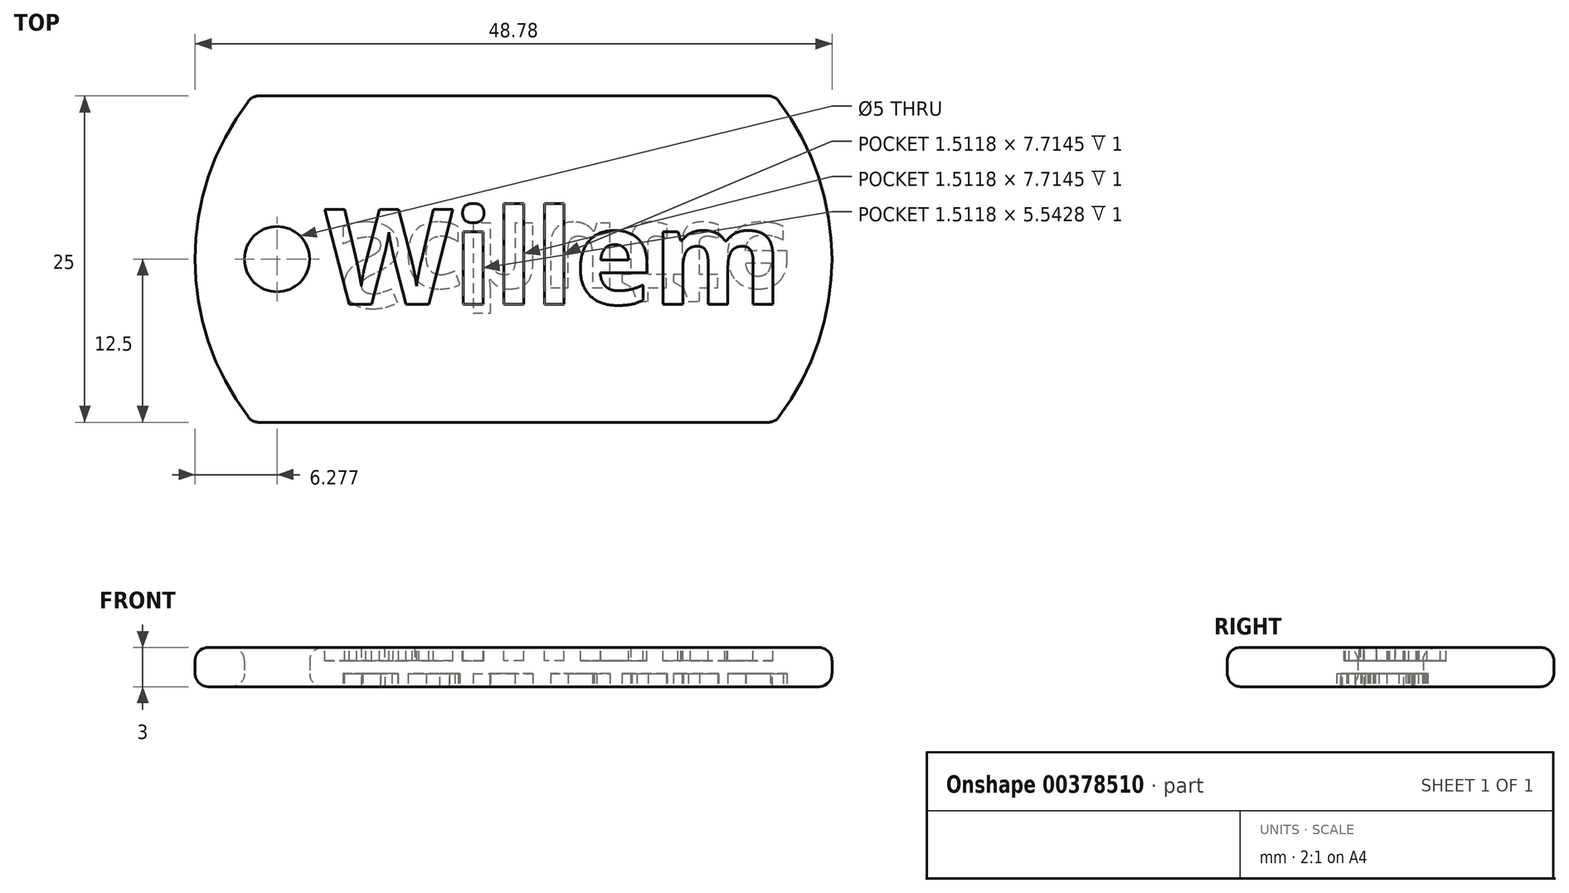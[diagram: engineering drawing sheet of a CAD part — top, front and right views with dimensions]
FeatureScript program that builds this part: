
annotation { "Feature Type Name" : "Feature", "Feature Type Description" : "" }
export const myFeature = defineFeature(function(context is Context, id is Id, definition is map)
    precondition{}
    {
        {
            var Q0;
            Q0=qCreatedBy(makeId("Top.planeOp"),FACE);
            var sketch = newSketch(context, id + "F0", { "sketchPlane" : qUnion([Q0])});
            skLineSegment(sketch, "E0.bottom", {"start": v(-20, 12.5) * mm, "end": v(20, 12.5) * mm});
            skLineSegment(sketch, "E0.top", {"start": v(-20, -12.5) * mm, "end": v(20, -12.5) * mm});
            skArc(sketch, "E1", {"start": v(-20, 12.5) * mm, "mid": v(-24.39, 0) * mm, "end": v(-20, -12.5) * mm});
            skArc(sketch, "E2", {"start": v(20, -12.5) * mm, "mid": v(24.39, 0) * mm, "end": v(20, 12.5) * mm});
            skCircle(sketch, "E3", {"center": v(-18.11, 0) * mm, "radius": 2.5 * mm});
            skSolve(sketch);
        }
        {
            var Q0;
            Q0=makeQuery(id+"F0.imprint","IMPRINT",FACE,{"disambiguationData":[TD([[makeQuery(id+"F0.imprint","IMPRINT",EDGE,{"derivedFrom":sQuery(id+"F0.wireOp",EDGE,"E0.bottom")}),-1.0]])]});
            extrude(context, id + "F1", {"entities" : qUnion([Q0]), "depth" : 3 * mm});
        }
        {
            var Q0;
            Q0=makeQuery(id+"F1.opExtrude","CAP_FACE",FACE,{"disambiguationData":[OSD([sQuery(id+"F0.wireOp",EDGE,"E0.bottom"),sQuery(id+"F0.wireOp",EDGE,"E0.top"),sQuery(id+"F0.wireOp",EDGE,"E1"),sQuery(id+"F0.wireOp",EDGE,"E2"),sQuery(id+"F0.wireOp",EDGE,"E3")])],"isStart":false});
            var sketch = newSketch(context, id + "F2", { "sketchPlane" : qUnion([Q0])});
            skText(sketch, "E4", { "text": "Willem\n", "fontName": "OpenSans-Bold.ttf"});
            const initialGuessF2  = {"E4": [-0.01445, -0.00345, 1, 0, 0.00731]};
            skSetInitialGuess(sketch, initialGuessF2);
            skSolve(sketch);
        }
        {
            var Q0;
            Q0=qSketchRegion(id+"F2",true);
            extrude(context, id + "F3", {"entities" : qUnion([Q0]), "operationType" : NewBodyOperationType.REMOVE, "oppositeDirection" : true, "depth" : 1 * mm});
        }
        {
            var Q0;
            Q0=makeQuery(id+"F1.opExtrude","CAP_FACE",FACE,{"disambiguationData":[OSD([sQuery(id+"F0.wireOp",EDGE,"E0.bottom"),sQuery(id+"F0.wireOp",EDGE,"E0.top"),sQuery(id+"F0.wireOp",EDGE,"E1"),sQuery(id+"F0.wireOp",EDGE,"E2"),sQuery(id+"F0.wireOp",EDGE,"E3")])],"isStart":true});
            var sketch = newSketch(context, id + "F4", { "sketchPlane" : qUnion([Q0])});
            skText(sketch, "E5", { "text": "Schutte", "fontName": "OpenSans-Bold.ttf"});
            const initialGuessF4  = {"E5": [-0.01347, -0.00276, 1, 0, 0.00653]};
            skSetInitialGuess(sketch, initialGuessF4);
            skSolve(sketch);
        }
        {
            var Q0;
            Q0=qSketchRegion(id+"F4",true);
            extrude(context, id + "F5", {"entities" : qUnion([Q0]), "operationType" : NewBodyOperationType.REMOVE, "oppositeDirection" : true, "depth" : 1 * mm});
        }
        {
            var Q0;
            Q0=makeQuery(id+"F1.opExtrude","SWEPT_FACE",FACE,{"disambiguationData":[OSD([sQuery(id+"F0.wireOp",EDGE,"E2")])]});
            var Q1;
            Q1=makeQuery(id+"F1.opExtrude","SWEPT_FACE",FACE,{"disambiguationData":[OSD([sQuery(id+"F0.wireOp",EDGE,"E0.top")])]});
            var Q2;
            Q2=makeQuery(id+"F1.opExtrude","SWEPT_FACE",FACE,{"disambiguationData":[OSD([sQuery(id+"F0.wireOp",EDGE,"E3")])]});
            var Q3;
            Q3=makeQuery(id+"F1.opExtrude","SWEPT_FACE",FACE,{"disambiguationData":[OSD([sQuery(id+"F0.wireOp",EDGE,"E1")])]});
            var Q4;
            Q4=makeQuery(id+"F1.opExtrude","SWEPT_FACE",FACE,{"disambiguationData":[OSD([sQuery(id+"F0.wireOp",EDGE,"E0.bottom")])]});
            fillet(context, id + "F6", {"entities" : qUnion([Q0, Q1, Q2, Q3, Q4]), "radius" : 1 * mm, "tangentPropagation" : true, "allowEdgeOverflow" : false});
        }
    });
